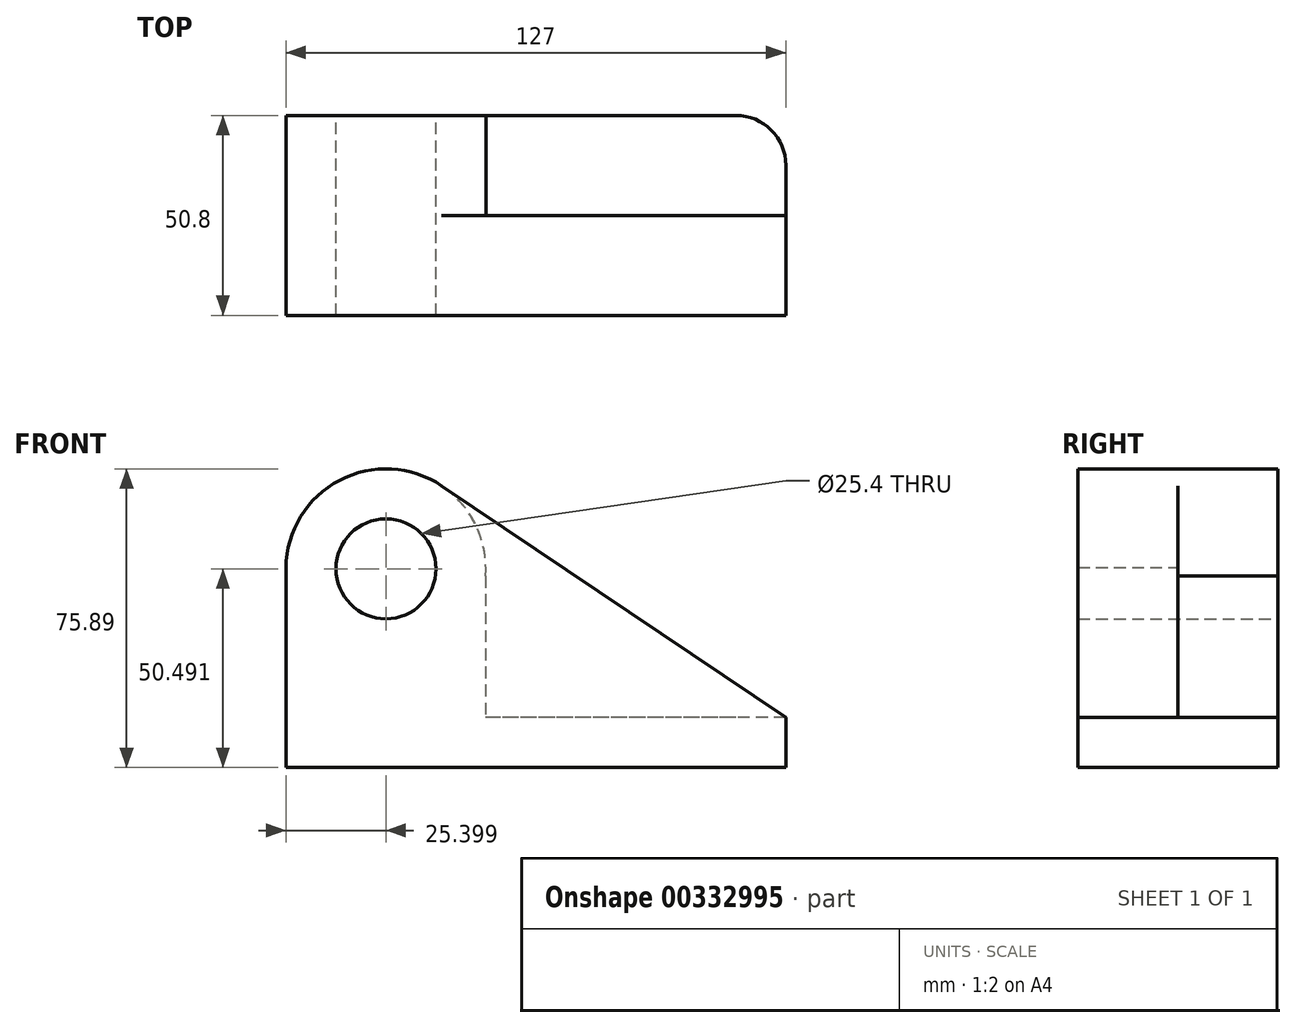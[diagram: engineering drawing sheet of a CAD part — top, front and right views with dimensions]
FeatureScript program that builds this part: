
annotation { "Feature Type Name" : "Feature", "Feature Type Description" : "" }
export const myFeature = defineFeature(function(context is Context, id is Id, definition is map)
    precondition{}
    {
        {
            var Q0;
            Q0=qCreatedBy(makeId("Front.planeOp"),FACE);
            var sketch = newSketch(context, id + "F0", { "sketchPlane" : qUnion([Q0])});
            skCircle(sketch, "E0", {"center": v(-75.2, 50.5) * mm, "radius": 12.7 * mm});
            skCircle(sketch, "E1", {"center": v(-75.2, 50.5) * mm, "radius": 25.4 * mm});
            skLineSegment(sketch, "E2", {"start": v(-100.59, 50.8) * mm, "end": v(-100.59, 0) * mm});
            skLineSegment(sketch, "E3", {"start": v(-100.59, 0) * mm, "end": v(26.41, 0) * mm});
            skLineSegment(sketch, "E4", {"start": v(26.41, 0) * mm, "end": v(26.41, 12.7) * mm});
            skLineSegment(sketch, "E5", {"start": v(26.41, 12.7) * mm, "end": v(-61, 71.56) * mm});
            skSolve(sketch);
        }
        {
            var Q0;
            {var subQ0=sQuery(id+"F0.wireOp",EDGE,"E3");Q0=makeQuery(id+"F0.imprint","IMPRINT",FACE,{"disambiguationData":[TD([[makeQuery(id+"F0.imprint","IMPRINT",EDGE,{"derivedFrom":subQ0}),1.0]])]});}
            var Q1;
            Q1=makeQuery(id+"F0.imprint","IMPRINT",FACE,{"disambiguationData":[TD([[makeQuery(id+"F0.imprint","IMPRINT",EDGE,{"derivedFrom":sQuery(id+"F0.wireOp",EDGE,"E0")}),-1.0]])]});
            extrude(context, id + "F1", {"entities" : qUnion([Q0, Q1]), "depth" : 25.4 * mm});
        }
        {
            var Q0;
            Q0=makeQuery(id+"F1.opExtrude","CAP_FACE",FACE,{"disambiguationData":[OSD([sQuery(id+"F0.wireOp",EDGE,"E0"),sQuery(id+"F0.wireOp",EDGE,"E1"),sQuery(id+"F0.wireOp",EDGE,"E2"),sQuery(id+"F0.wireOp",EDGE,"E3"),sQuery(id+"F0.wireOp",EDGE,"E4"),sQuery(id+"F0.wireOp",EDGE,"E5")])],"isStart":true});
            var sketch = newSketch(context, id + "F2", { "sketchPlane" : qUnion([Q0])});
            skCircle(sketch, "E6", {"center": v(75.2, 50.5) * mm, "radius": 12.7 * mm});
            skArc(sketch, "E7", {"start": v(100.52, 48.66) * mm, "mid": v(75.2, 75.9) * mm, "end": v(49.86, 48.66) * mm});
            skLineSegment(sketch, "E8.bottom", {"start": v(-26.41, 12.7) * mm, "end": v(49.86, 12.7) * mm});
            skLineSegment(sketch, "E8.top", {"start": v(-26.41, 0) * mm, "end": v(100.59, 0) * mm});
            skLineSegment(sketch, "E8.left", {"start": v(-26.41, 12.7) * mm, "end": v(-26.41, 0) * mm});
            skLineSegment(sketch, "E8.right", {"start": v(100.59, 12.7) * mm, "end": v(100.59, 0) * mm});
            skLineSegment(sketch, "E9", {"start": v(100.52, 48.66) * mm, "end": v(100.59, 12.7) * mm});
            skLineSegment(sketch, "E10", {"start": v(49.86, 48.66) * mm, "end": v(49.86, 12.7) * mm});
            skSolve(sketch);
        }
        {
            var Q0;
            Q0 = qSketchRegion(id + "F2", true);
            extrude(context, id + "F3", {"entities" : qUnion([Q0]), "operationType" : NewBodyOperationType.ADD, "depth" : 25.4 * mm});
        }
        {
            var Q0;
            Q0=makeQuery(id+"F3.opExtrude","CAP_EDGE",EDGE,{"disambiguationData":[OSD([sQuery(id+"F2.wireOp",EDGE,"E8.left")])],"isStart":false});
            fillet(context, id + "F4", {"entities" : qUnion([Q0]), "radius" : 12.7 * mm, "tangentPropagation" : true, "allowEdgeOverflow" : false});
        }
    });
